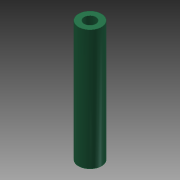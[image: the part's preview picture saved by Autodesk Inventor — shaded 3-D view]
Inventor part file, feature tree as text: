
AUTODESK INVENTOR PART (.ipt)
format: ipt  version: 2015 (Build 190159000, 159)  size: 72,704 bytes
history: native  units: in
note: dims shown in document units (in); Inventor stores cm internally (conversion verified against a paired STEP export)
features: extrude x1, sketch x1
ambient origin geometry x8: Origin, YZ Plane, XZ Plane, XY Plane, X Axis, Y Axis, Z Axis, Center Point
bodies: Solid1 (feature_tree)
feature tree (2):
  extrude  "Extrusion1"  Depth=1.5748in
  sketch  "Sketch1"  dims[d0=0.3in d1=0.155in d2=1.5748in d3=0.0in]
